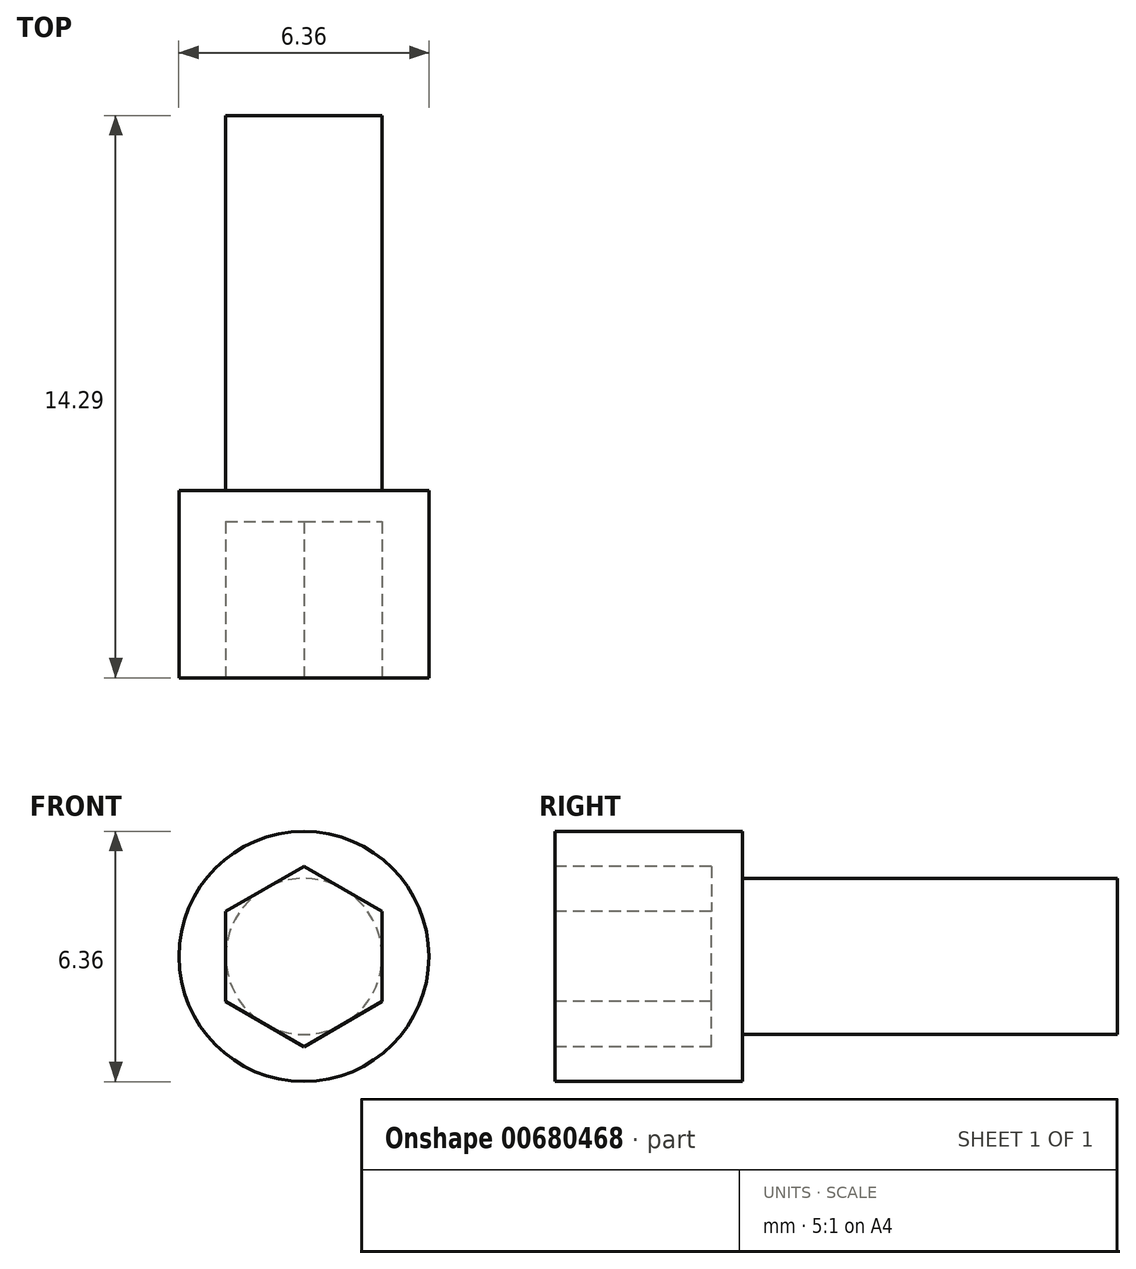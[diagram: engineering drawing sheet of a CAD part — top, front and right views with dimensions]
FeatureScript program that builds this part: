
annotation { "Feature Type Name" : "Feature", "Feature Type Description" : "" }
export const myFeature = defineFeature(function(context is Context, id is Id, definition is map)
    precondition{}
    {
        {
            var Q0;
            Q0=qCreatedBy(makeId("Front.planeOp"),FACE);
            var sketch = newSketch(context, id + "F0", { "sketchPlane" : qUnion([Q0])});
            skCircle(sketch, "E0", {"center": v(0, 0) * mm, "radius": 1.98 * mm});
            skSolve(sketch);
        }
        {
            var Q0;
            Q0=makeQuery(id+"F0.imprint","IMPRINT",FACE,{"disambiguationData":[TD([[makeQuery(id+"F0.imprint","IMPRINT",EDGE,{"derivedFrom":sQuery(id+"F0.wireOp",EDGE,"E0")}),1.0]])]});
            extrude(context, id + "F1", {"entities" : qUnion([Q0]), "depth" : 9.52 * mm, "offsetDistance" : 25.4 * mm});
        }
        {
            var Q0;
            Q0=makeQuery(id+"F1.opExtrude","CAP_FACE",FACE,{"disambiguationData":[OSD([sQuery(id+"F0.wireOp",EDGE,"E0")])],"isStart":false});
            var sketch = newSketch(context, id + "F2", { "sketchPlane" : qUnion([Q0])});
            skCircle(sketch, "E1.cCircle", {"center": v(0, 0) * mm, "radius": 3.18 * mm, "construction": true});
            skLineSegment(sketch, "E1.0", {"start": v(0, 3.67) * mm, "end": v(3.17, 1.83) * mm});
            skLineSegment(sketch, "E1.1", {"start": v(3.17, 1.83) * mm, "end": v(3.18, -1.83) * mm});
            skLineSegment(sketch, "E1.2", {"start": v(3.18, -1.83) * mm, "end": v(0, -3.67) * mm});
            skLineSegment(sketch, "E1.3", {"start": v(0, -3.67) * mm, "end": v(-3.18, -1.83) * mm});
            skLineSegment(sketch, "E1.4", {"start": v(-3.17, -1.83) * mm, "end": v(-3.17, 1.83) * mm});
            skLineSegment(sketch, "E1.5", {"start": v(-3.17, 1.83) * mm, "end": v(0, 3.67) * mm});
            skPoint(sketch, "E1.0.midPoint", {"position": v(1.59, 2.75) * mm});
            skSolve(sketch);
        }
        {
            var Q0;
            Q0=makeQuery(id+"F2.imprint","IMPRINT",FACE,{"disambiguationData":[TD([[makeQuery(id+"F2.imprint","IMPRINT",EDGE,{"derivedFrom":makeQuery(id+"F1.opExtrude","CAP_EDGE",EDGE,{"disambiguationData":[OSD([sQuery(id+"F0.wireOp",EDGE,"E0")])],"isStart":false})}),1.0]])]});
            var sketch = newSketch(context, id + "F3", { "sketchPlane" : qUnion([Q0])});
            skCircle(sketch, "E2.0", {"center": v(0, 0) * mm, "radius": 3.18 * mm});
            skSolve(sketch);
        }
        {
            var Q0;
            Q0=qSketchRegion(id+"F3",true);
            extrude(context, id + "F4", {"entities" : qUnion([Q0]), "operationType" : NewBodyOperationType.ADD, "depth" : 4.76 * mm, "offsetDistance" : 25.4 * mm});
        }
        {
            var Q0;
            Q0=makeQuery(id+"F4.opExtrude","CAP_FACE",FACE,{"disambiguationData":[OSD([sQuery(id+"F3.wireOp",EDGE,"E2.0")])],"isStart":false});
            var sketch = newSketch(context, id + "F5", { "sketchPlane" : qUnion([Q0])});
            skCircle(sketch, "E3.cCircle", {"center": v(0, 0) * mm, "radius": 1.98 * mm, "construction": true});
            skLineSegment(sketch, "E3.0", {"start": v(0, 2.3) * mm, "end": v(1.98, 1.15) * mm});
            skLineSegment(sketch, "E3.1", {"start": v(1.98, 1.15) * mm, "end": v(1.98, -1.15) * mm});
            skLineSegment(sketch, "E3.2", {"start": v(1.98, -1.15) * mm, "end": v(0, -2.3) * mm});
            skLineSegment(sketch, "E3.3", {"start": v(0, -2.3) * mm, "end": v(-1.98, -1.15) * mm});
            skLineSegment(sketch, "E3.4", {"start": v(-1.98, -1.15) * mm, "end": v(-1.98, 1.15) * mm});
            skLineSegment(sketch, "E3.5", {"start": v(-1.98, 1.15) * mm, "end": v(0, 2.3) * mm});
            skPoint(sketch, "E3.0.midPoint", {"position": v(1, 1.72) * mm});
            skSolve(sketch);
        }
        {
            var Q0;
            Q0=makeQuery(id+"F5.imprint","IMPRINT",FACE,{"disambiguationData":[TD([[makeQuery(id+"F5.imprint","IMPRINT",EDGE,{"derivedFrom":sQuery(id+"F5.wireOp",EDGE,"E3.0")}),-1.0]])]});
            extrude(context, id + "F6", {"entities" : qUnion([Q0]), "operationType" : NewBodyOperationType.REMOVE, "oppositeDirection" : true, "depth" : 3.97 * mm, "offsetDistance" : 25.4 * mm});
        }
    });
